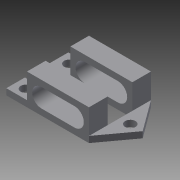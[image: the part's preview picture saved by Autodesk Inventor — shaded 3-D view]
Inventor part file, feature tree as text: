
AUTODESK INVENTOR PART (.ipt)
format: ipt  version: 2015 (Build 190159000, 159)  size: 141,824 bytes
history: native  units: in
note: dims shown in document units (in); Inventor stores cm internally (conversion verified against a paired STEP export)
features: extrude x3, sketch x2
ambient origin geometry x8: Origin, YZ Plane, XZ Plane, XY Plane, X Axis, Y Axis, Z Axis, Center Point
bodies: Solid1 (feature_tree)
feature tree (5):
  sketch  "Sketch1"  dims[d0=0.252in d1=0.2677in]
  extrude  "Extrusion1"  Depth=0.2677in
  extrude  "Extrusion2"  Depth=0.4724in
  extrude  "Extrusion3"  Depth=0.5906in
  sketch  "Sketch2"  dims[d2=0.3937in d3=0.4724in d4=0.5906in d5=0.5906in d6=0.3543in d7=0.2953in d8=0.3937in d9=0.1969in d10=0.3937in d11=0.3937in d12=0.1969in d13=0.1969in d14=0.1969in d15=1.1811in d17=0.2362in d18=0.1969in d19=0.1181in d20=0.0in d21=0.5906in d22=0.0in d23=0.2953in d24=0.2756in d25=0.3543in d26=0.2756in d27=0.3543in d28=1.2205in d29=0.0in]
